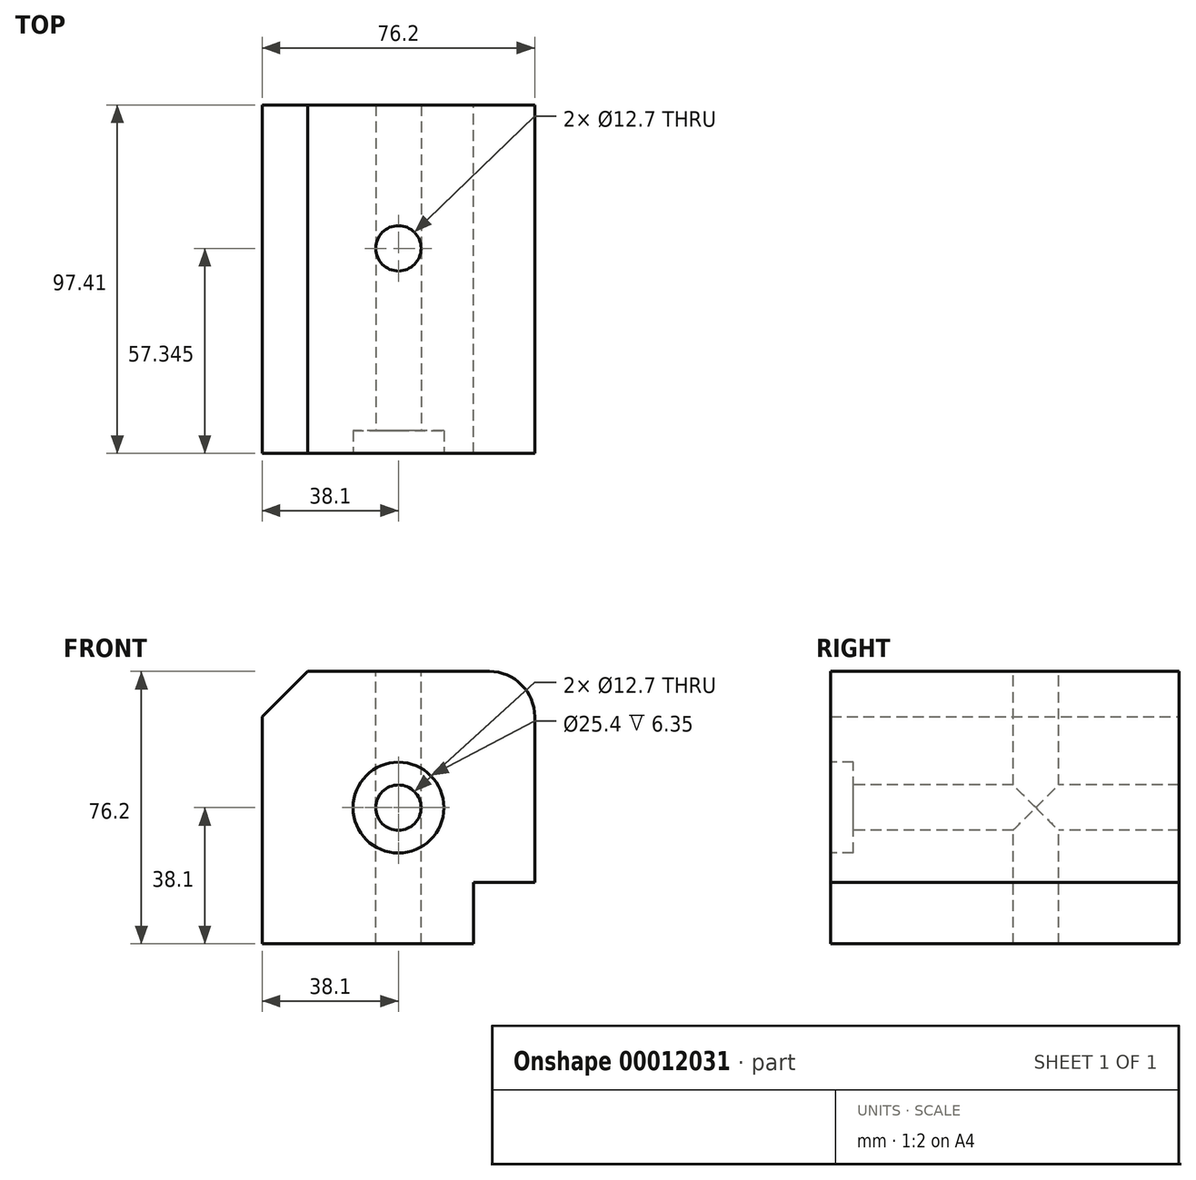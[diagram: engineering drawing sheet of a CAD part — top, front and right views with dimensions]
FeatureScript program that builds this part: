
annotation { "Feature Type Name" : "Feature", "Feature Type Description" : "" }
export const myFeature = defineFeature(function(context is Context, id is Id, definition is map)
    precondition{}
    {
        {
            var Q0;
            Q0=qCreatedBy(makeId("Front.planeOp"),FACE);
            var sketch = newSketch(context, id + "F0", { "sketchPlane" : qUnion([Q0])});
            skLineSegment(sketch, "E0.rect.bottom", {"start": v(38.1, 38.1) * mm, "end": v(-38.1, 38.1) * mm});
            skLineSegment(sketch, "E0.rect.top", {"start": v(38.1, -38.1) * mm, "end": v(-38.1, -38.1) * mm});
            skLineSegment(sketch, "E0.rect.left", {"start": v(38.1, 38.1) * mm, "end": v(38.1, -38.1) * mm});
            skLineSegment(sketch, "E0.rect.right", {"start": v(-38.1, 38.1) * mm, "end": v(-38.1, -38.1) * mm});
            skPoint(sketch, "E0.rect.middle", {"position": v(0, 0) * mm});
            skSolve(sketch);
        }
        {
            var Q0;
            Q0=makeQuery(id+"F0.imprint","IMPRINT",FACE,{"disambiguationData":[TD([[makeQuery(id+"F0.imprint","IMPRINT",EDGE,{"derivedFrom":sQuery(id+"F0.wireOp",EDGE,"E0.rect.bottom")}),1.0]])]});
            extrude(context, id + "F1", {"entities" : qUnion([Q0]), "depth" : 97.4 * mm});
        }
        {
            var Q0;
            Q0=makeQuery(id+"F1.opExtrude","SWEPT_EDGE",EDGE,{"disambiguationData":[OSD([sQuery(id+"F0.wireOp",EDGE,"E0.rect.bottom"),sQuery(id+"F0.wireOp",EDGE,"E0.rect.left")])]});
            fillet(context, id + "F2", {"entities" : qUnion([Q0]), "radius" : 12.7 * mm, "tangentPropagation" : true, "allowEdgeOverflow" : false});
        }
        {
            var Q0;
            Q0=makeQuery(id+"F1.opExtrude","SWEPT_EDGE",EDGE,{"disambiguationData":[OSD([sQuery(id+"F0.wireOp",EDGE,"E0.rect.bottom"),sQuery(id+"F0.wireOp",EDGE,"E0.rect.right")])]});
            chamfer(context, id + "F3", {"entities" : qUnion([Q0]), "width" : 12.7 * mm, "tangentPropagation" : true});
        }
        {
            var Q0;
            Q0=makeQuery(id+"F1.opExtrude","CAP_FACE",FACE,{"disambiguationData":[OSD([sQuery(id+"F0.wireOp",EDGE,"E0.rect.bottom"),sQuery(id+"F0.wireOp",EDGE,"E0.rect.top"),sQuery(id+"F0.wireOp",EDGE,"E0.rect.left"),sQuery(id+"F0.wireOp",EDGE,"E0.rect.right")])],"isStart":false});
            var sketch = newSketch(context, id + "F4", { "sketchPlane" : qUnion([Q0])});
            skPoint(sketch, "E1", {"position": v(0, 0) * mm});
            skSolve(sketch);
        }
        {
            var Q0;
            Q0=sQuery(id+"F4.wireOp",VERTEX,"E1");
            var Q1;
            Q1=makeQuery(id+"F1.opExtrude","SWEPT_BODY",BODY,{"disambiguationData":[OSD([sQuery(id+"F0.wireOp",EDGE,"E0.rect.bottom"),sQuery(id+"F0.wireOp",EDGE,"E0.rect.top"),sQuery(id+"F0.wireOp",EDGE,"E0.rect.left"),sQuery(id+"F0.wireOp",EDGE,"E0.rect.right")])]});
            hole(context, id + "F5", {"style" : HoleStyle.C_BORE, "holeDiameter" : 12.7 * mm, "cBoreDiameter" : 25.4 * mm, "cBoreDepth" : 6.35 * mm, "endStyle" : HoleEndStyle.THROUGH, "locations" : qUnion([Q0]), "scope" : qUnion([Q1])});
        }
        {
            var Q0;
            Q0=qCreatedBy(makeId("Front.planeOp"),FACE);
            var sketch = newSketch(context, id + "F6", { "sketchPlane" : qUnion([Q0])});
            skPoint(sketch, "E2.0", {"position": v(38.1, -38.1) * mm});
            skLineSegment(sketch, "E3.bottom", {"start": v(38.1, -38.1) * mm, "end": v(21.03, -38.1) * mm});
            skLineSegment(sketch, "E3.top", {"start": v(38.1, -20.92) * mm, "end": v(21.03, -20.92) * mm});
            skLineSegment(sketch, "E3.left", {"start": v(38.1, -38.1) * mm, "end": v(38.1, -20.92) * mm});
            skLineSegment(sketch, "E3.right", {"start": v(21.03, -38.1) * mm, "end": v(21.03, -20.92) * mm});
            skSolve(sketch);
        }
        {
            var Q0;
            Q0=makeQuery(id+"F6.imprint","IMPRINT",FACE,{"disambiguationData":[TD([[makeQuery(id+"F6.imprint","IMPRINT",EDGE,{"derivedFrom":sQuery(id+"F6.wireOp",EDGE,"E3.bottom")}),-1.0]])]});
            extrude(context, id + "F7", {"entities" : qUnion([Q0]), "operationType" : NewBodyOperationType.REMOVE, "endBound" : BoundingType.THROUGH_ALL, "depth" : 25.4 * mm});
        }
        {
            var Q0;
            Q0=makeQuery(id+"F1.opExtrude","SWEPT_FACE",FACE,{"disambiguationData":[OSD([sQuery(id+"F0.wireOp",EDGE,"E0.rect.bottom")])]});
            var sketch = newSketch(context, id + "F8", { "sketchPlane" : qUnion([Q0])});
            skPoint(sketch, "E4", {"position": v(0, -40.06) * mm});
            skSolve(sketch);
        }
        {
            var Q0;
            Q0=sQuery(id+"F8.wireOp",VERTEX,"E4");
            var Q1;
            Q1=makeQuery(id+"F1.opExtrude","SWEPT_BODY",BODY,{"disambiguationData":[OSD([sQuery(id+"F0.wireOp",EDGE,"E0.rect.bottom"),sQuery(id+"F0.wireOp",EDGE,"E0.rect.top"),sQuery(id+"F0.wireOp",EDGE,"E0.rect.left"),sQuery(id+"F0.wireOp",EDGE,"E0.rect.right")])]});
            hole(context, id + "F9", {"style" : HoleStyle.SIMPLE, "holeDiameter" : 12.7 * mm, "endStyle" : HoleEndStyle.THROUGH, "locations" : qUnion([Q0]), "scope" : qUnion([Q1])});
        }
    });
